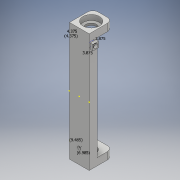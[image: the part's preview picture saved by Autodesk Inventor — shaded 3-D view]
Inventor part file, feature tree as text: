
AUTODESK INVENTOR PART (.ipt)
format: ipt  version: 2018 (Build 220112000, 112)  size: 439,808 bytes
history: native  units: mm
features: sketch x21, extrude x12, fillet x3
ambient origin geometry x8: Origin, YZ Plane, XZ Plane, XY Plane, X Axis, Y Axis, Z Axis, Center Point
bodies: Solid1 (feature_tree)
feature tree (36):
  extrude  "Extrusion1"  Depth=100.0mm
  sketch  "Sketch2"  dims[d2=2.0mm d3=0.0mm d4=2.5mm]
  sketch  "Sketch3"  dims[d5=2.5mm d6=10.89mm d7=0.0mm]
  extrude  "Extrusion2"  Depth=2.5mm
  extrude  "Extrusion3"  Depth=10.89mm TaperAngle=0.0deg
  extrude  "Extrusion4"  Depth=2.14mm TaperAngle=0.0deg
  extrude  "Extrusion5"  Depth=2.14mm TaperAngle=0.0deg
  fillet  "Fillet1"  Radius=7.0mm
  extrude  "Extrusion6"  Depth=22.5mm
  extrude  "Extrusion7"  Depth=7.0mm TaperAngle=0.0deg
  fillet  "Fillet2"  Radius=7.0mm
  extrude  "Extrusion8"  Depth=5.0mm
  extrude  "Extrusion9"  Depth=2.0mm TaperAngle=0.0deg
  sketch  "Sketch12"  dims[d35=2.0mm d36=6.985mm]
  extrude  "Extrusion10"  Depth=2.0mm TaperAngle=0.0deg
  fillet  "Fillet3"  Radius=13.97mm
  sketch  "Sketch14"  dims[d38=7.75mm]
  sketch  "Sketch15"  dims[d39=5.5mm]
  extrude  "Extrusion11"  Depth=2.0mm TaperAngle=0.0deg
  sketch  "Sketch17"  dims[d41=4.0mm]
  sketch  "Sketch18"  dims[d42=2.5mm d43=0.0mm]
  sketch  "Sketch19"  dims[d44=3.875mm]
  extrude  "Extrusion12"  Depth=2.0mm
  sketch  "Sketch21"  dims[d46=8.75mm d47=3.0mm d48=3.0mm d49=0.0mm d50=4.375mm d51=4.375mm]
  sketch  "Sketch1"  dims[d0=13.97mm d1=100.0mm]
  sketch  "Sketch4"  dims[d8=3.14mm d9=0.0mm d10=2.14mm d11=0.0mm]
  sketch  "Sketch5"  dims[d12=3.5mm d13=2.14mm d14=0.0mm d15=7.0mm]
  sketch  "Sketch6"  dims[d16=11.43mm d17=22.5mm]
  sketch  "Sketch7"  dims[d18=15.975mm d19=7.0mm d20=0.0mm d21=7.0mm d22=0.0mm]
  sketch  "Sketch8"  dims[d23=5.0mm d24=6.35mm]
  sketch  "Sketch9"  dims[d25=10.0mm d26=2.0mm d27=0.0mm]
  sketch  "Sketch10"  dims[d28=10.0mm d29=2.0mm d30=0.0mm d31=13.97mm]
  sketch  "Sketch11"  dims[d32=3.175mm d33=2.0mm d34=0.0mm]
  sketch  "Sketch13"  dims[d37=9.485mm]
  sketch  "Sketch16"  dims[d40=5.5mm]
  sketch  "Sketch20"  dims[d45=3.875mm]
